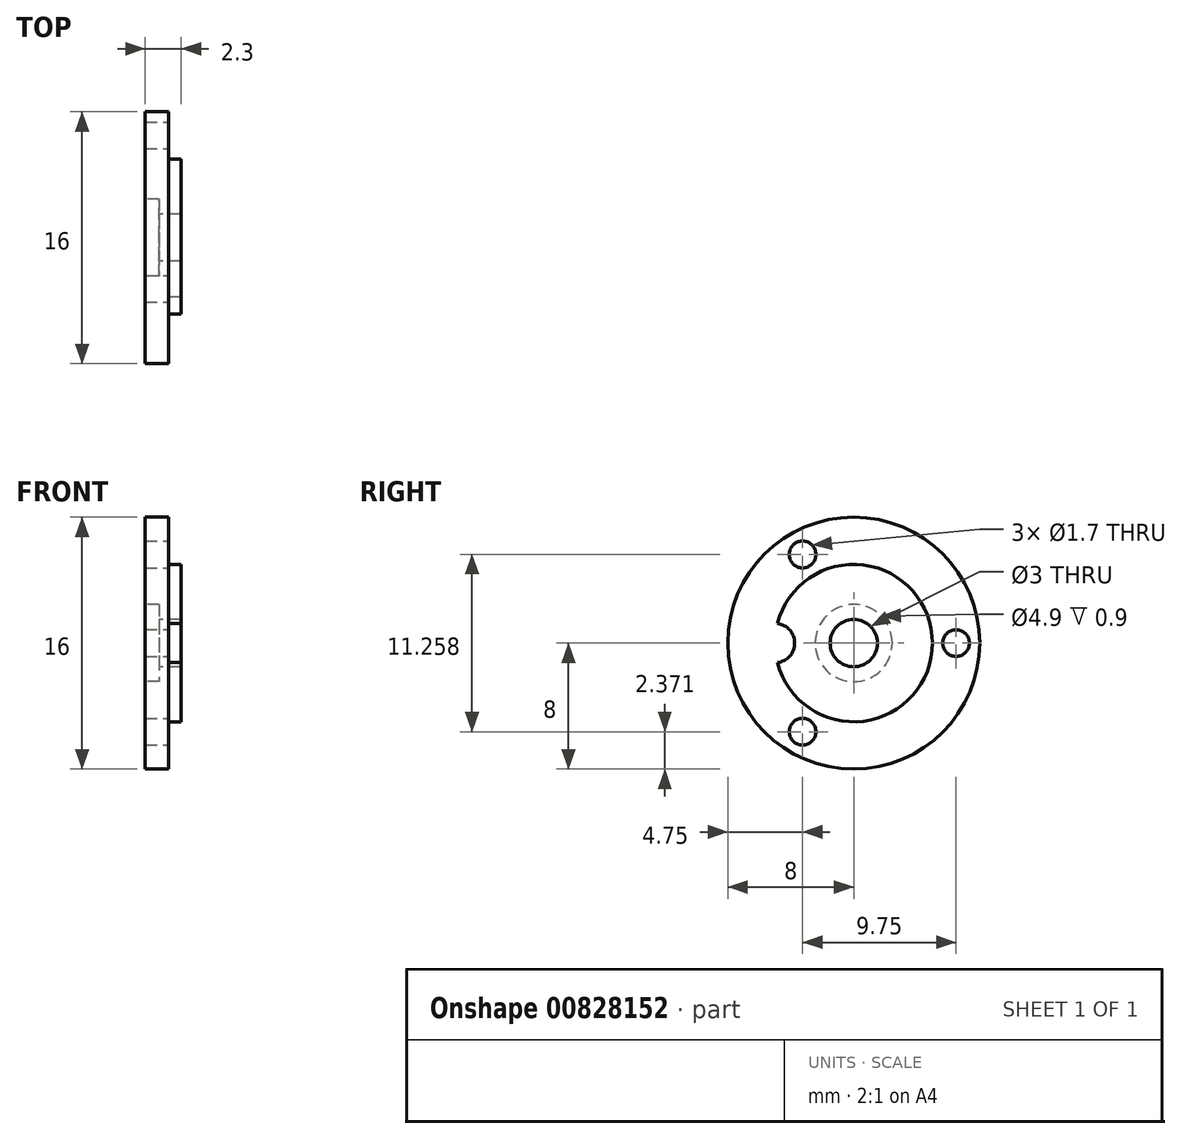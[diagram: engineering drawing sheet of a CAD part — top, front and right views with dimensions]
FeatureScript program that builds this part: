
annotation { "Feature Type Name" : "Feature", "Feature Type Description" : "" }
export const myFeature = defineFeature(function(context is Context, id is Id, definition is map)
    precondition{}
    {
        {
            var Q0;
            Q0=qCreatedBy(makeId("Front.planeOp"),FACE);
            var sketch = newSketch(context, id + "F0", { "sketchPlane" : qUnion([Q0])});
            skLineSegment(sketch, "E0", {"start": v(0, 0) * mm, "end": v(2.3, 0) * mm});
            skLineSegment(sketch, "E1", {"start": v(2.3, 0) * mm, "end": v(2.3, 5) * mm});
            skLineSegment(sketch, "E2", {"start": v(2.3, 5) * mm, "end": v(1.5, 5) * mm});
            skLineSegment(sketch, "E3", {"start": v(1.5, 5) * mm, "end": v(1.5, 8) * mm});
            skLineSegment(sketch, "E4", {"start": v(1.5, 8) * mm, "end": v(0, 8) * mm});
            skLineSegment(sketch, "E5", {"start": v(0, 8) * mm, "end": v(0, 0) * mm});
            skSolve(sketch);
        }
        {
            var Q0;
            Q0 = qSketchRegion(id + "F0", true);
            var Q1;
            Q1=sQuery(id+"F0.wireOp",EDGE,"E0");
            revolve(context, id + "F1", {"surfaceOperationType" : NewSurfaceOperationType.NEW, "entities" : qUnion([Q0]), "axis" : qUnion([Q1]), "revolveType" : RevolveType.FULL});
        }
        {
            var Q0;
            Q0=qCreatedBy(makeId("Front.planeOp"),FACE);
            var sketch = newSketch(context, id + "F2", { "sketchPlane" : qUnion([Q0])});
            skLineSegment(sketch, "E6", {"start": v(0, 0) * mm, "end": v(0, 2.45) * mm});
            skLineSegment(sketch, "E7", {"start": v(0, 2.45) * mm, "end": v(0.9, 2.45) * mm});
            skLineSegment(sketch, "E8", {"start": v(0.9, 2.45) * mm, "end": v(0.9, 1.5) * mm});
            skLineSegment(sketch, "E9", {"start": v(0.9, 1.5) * mm, "end": v(2.3, 1.5) * mm});
            skLineSegment(sketch, "E10", {"start": v(2.3, 1.5) * mm, "end": v(2.3, 0) * mm});
            skLineSegment(sketch, "E11", {"start": v(2.3, 0) * mm, "end": v(0, 0) * mm});
            skSolve(sketch);
        }
        {
            var Q0;
            Q0 = qSketchRegion(id + "F2", true);
            var Q1;
            Q1=sQuery(id+"F2.wireOp",EDGE,"E11");
            revolve(context, id + "F3", {"operationType" : NewBodyOperationType.REMOVE, "surfaceOperationType" : NewSurfaceOperationType.NEW, "entities" : qUnion([Q0]), "axis" : qUnion([Q1]), "revolveType" : RevolveType.FULL, "oppositeDirection" : true});
        }
        {
            var Q0;
            Q0=makeQuery(id+"F1.opRevolve","SWEPT_FACE",FACE,{"disambiguationData":[OSD([sQuery(id+"F0.wireOp",EDGE,"E3")])]});
            var sketch = newSketch(context, id + "F4", { "sketchPlane" : qUnion([Q0])});
            skCircle(sketch, "E12", {"center": v(0, 0) * mm, "radius": 6.5 * mm, "construction": true});
            skLineSegment(sketch, "E13", {"start": v(0, 0) * mm, "end": v(6.5, 0) * mm});
            skLineSegment(sketch, "E14", {"start": v(0, 0) * mm, "end": v(-3.25, -5.63) * mm});
            skLineSegment(sketch, "E15", {"start": v(0, 0) * mm, "end": v(-3.25, 5.63) * mm});
            skCircle(sketch, "E16", {"center": v(-3.25, 5.63) * mm, "radius": 0.85 * mm});
            skCircle(sketch, "E17", {"center": v(6.5, 0) * mm, "radius": 0.85 * mm});
            skCircle(sketch, "E18", {"center": v(-3.25, -5.63) * mm, "radius": 0.85 * mm});
            skSolve(sketch);
        }
        {
            var Q0;
            Q0 = qSketchRegion(id + "F4", true);
            extrude(context, id + "F5", {"entities" : qUnion([Q0]), "operationType" : NewBodyOperationType.REMOVE, "endBound" : BoundingType.THROUGH_ALL, "oppositeDirection" : true, "depth" : 25 * mm, "offsetDistance" : 25 * mm});
        }
        {
            var Q0;
            Q0=makeQuery(id+"F1.opRevolve","SWEPT_FACE",FACE,{"disambiguationData":[OSD([sQuery(id+"F0.wireOp",EDGE,"E1")])]});
            var sketch = newSketch(context, id + "F6", { "sketchPlane" : qUnion([Q0])});
            skCircle(sketch, "E19", {"center": v(-5, 0) * mm, "radius": 1.25 * mm});
            skSolve(sketch);
        }
        {
            var Q0;
            Q0 = qSketchRegion(id + "F6", true);
            var Q1;
            Q1=makeQuery(id+"F1.opRevolve","SWEPT_FACE",FACE,{"disambiguationData":[OSD([sQuery(id+"F0.wireOp",EDGE,"E3")])]});
            extrude(context, id + "F7", {"entities" : qUnion([Q0]), "operationType" : NewBodyOperationType.REMOVE, "endBound" : BoundingType.UP_TO_SURFACE, "oppositeDirection" : true, "depth" : 25 * mm, "endBoundEntityFace" : qUnion([Q1]), "offsetDistance" : 25 * mm});
        }
    });
